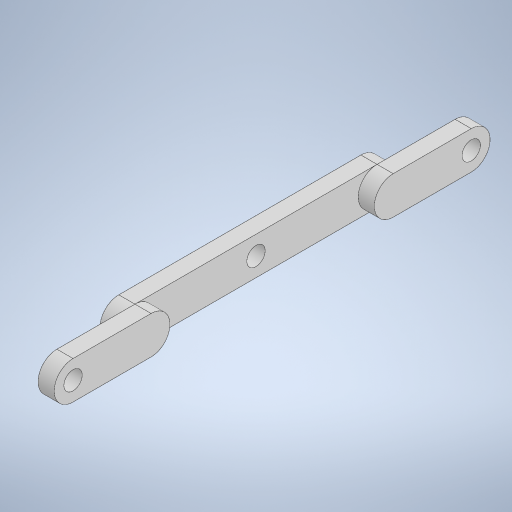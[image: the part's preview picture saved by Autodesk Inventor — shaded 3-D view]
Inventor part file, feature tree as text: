
AUTODESK INVENTOR PART (.ipt)
format: ipt  version: 2024.3 (Build 283343000, 343)  size: 299,520 bytes
history: native  units: mm
features: extrude x5, sketch x4, hole x2
ambient origin geometry x8: Origin, YZ Plane, XZ Plane, XY Plane, X Axis, Y Axis, Z Axis, Center Point
bodies: Body1 (feature_tree)
feature tree (11):
  sketch  "Sketch1"  dims[d17=5.0mm d18=81.0mm]
  extrude  "Extrusión3"  Depth=81.0mm
  extrude  "Extrusión4"  Depth=7.0mm
  extrude  "Extrusión5"  Depth=16.0mm TaperAngle=0.0deg
  extrude  "Extrusión6"  Depth=10.0mm
  hole  "Agujero1"  [1 undecoded]
  hole  "Agujero2"  [1 undecoded]
  extrude  "Extrusión7"  Depth=10.0mm
  sketch  "Boceto2"  dims[d19=3.0mm d20=7.0mm]
  sketch  "Boceto3"  dims[d21=22.0mm d22=0.0mm d23=16.0mm d24=0.0mm]
  sketch  "Boceto4"  dims[d25=3.4mm d26=6.0mm d27=6.3mm d28=2.0mm d29=90.0deg d30=8.0mm d31=20.594885mm d32=45.0mm d33=16.0mm d34=0.0mm d35=10.0mm d36=0.0mm d37=3.4mm d38=6.0mm d39=6.3mm d40=2.0mm d41=90.0deg d42=8.0mm d43=20.594885mm d44=10.0mm d45=0.0mm]
note: 2 required parameter values undecoded (feature->parameter linkage not recoverable at this tier; creation-order binding heuristic only, values carry confidence <= 0.55)
